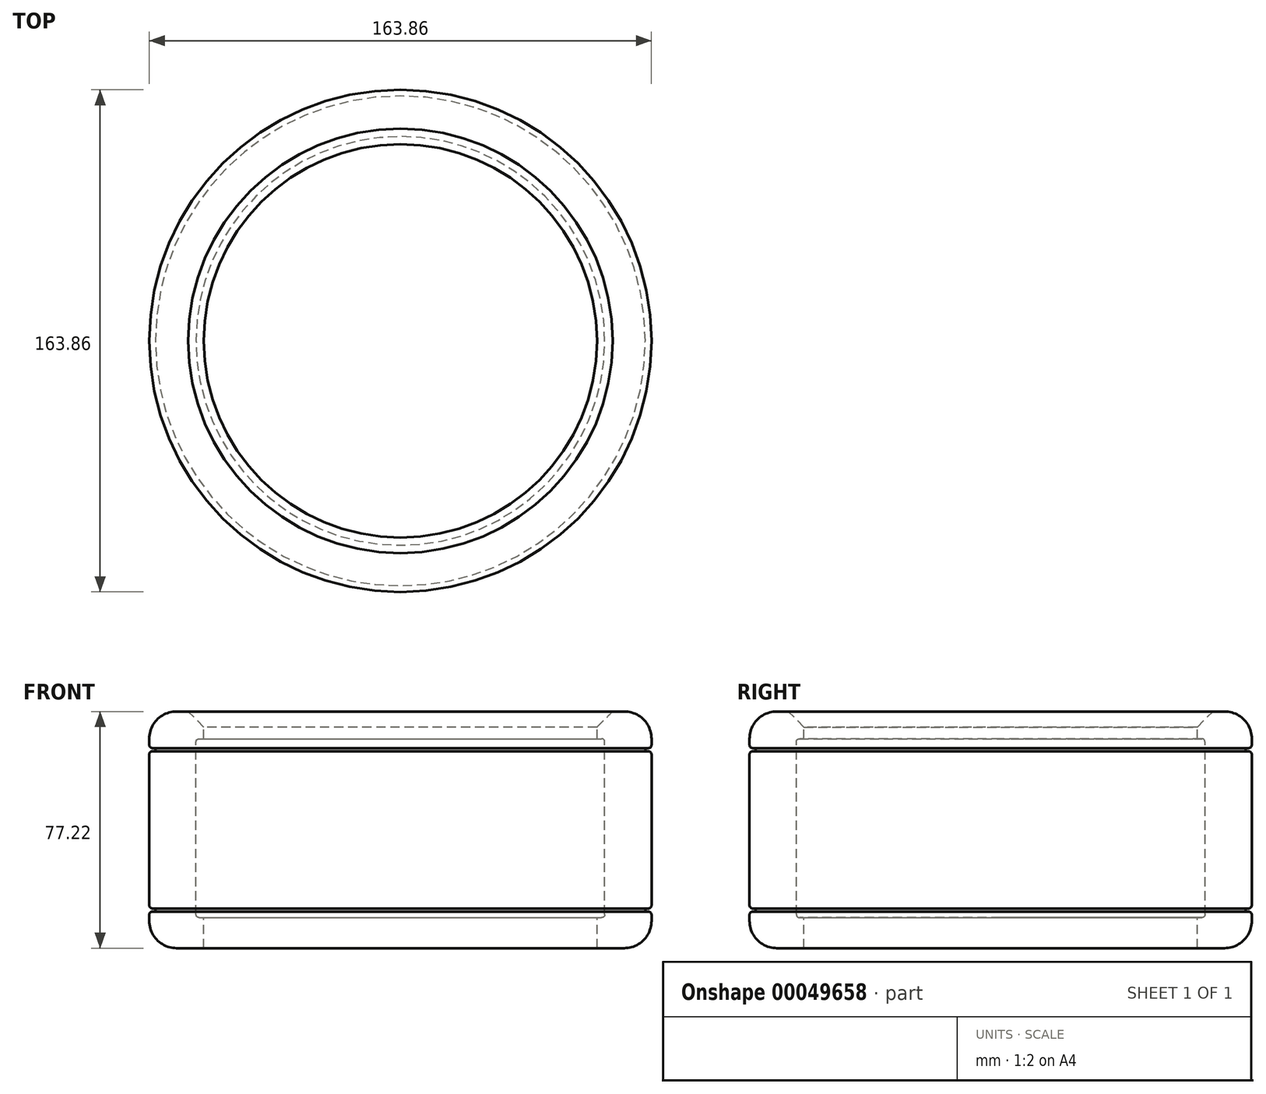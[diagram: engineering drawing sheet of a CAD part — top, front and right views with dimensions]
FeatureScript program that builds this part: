
annotation { "Feature Type Name" : "Feature", "Feature Type Description" : "" }
export const myFeature = defineFeature(function(context is Context, id is Id, definition is map)
    precondition{}
    {
        {
            var Q0;
            Q0=qCreatedBy(makeId("Top.planeOp"),FACE);
            var sketch = newSketch(context, id + "F0", { "sketchPlane" : qUnion([Q0])});
            skCircle(sketch, "E0", {"center": v(0, 0) * mm, "radius": 82.55 * mm});
            skSolve(sketch);
        }
        {
            var Q0;
            Q0=qCreatedBy(makeId("Front.planeOp"),FACE);
            var sketch = newSketch(context, id + "F1", { "sketchPlane" : qUnion([Q0])});
            skLineSegment(sketch, "E1.bottom", {"start": v(-73.04, 0) * mm, "end": v(-64.15, 0) * mm});
            skLineSegment(sketch, "E1.top", {"start": v(-73.04, 77.22) * mm, "end": v(-64.15, 77.22) * mm});
            skLineSegment(sketch, "E1.right", {"start": v(-64.15, 0) * mm, "end": v(-64.15, 9.97) * mm});
            skPoint(sketch, "E2.visualSharp", {"position": v(-81.93, 77.22) * mm});
            skArc(sketch, "E2.filletArc", {"start": v(-73.04, 77.22) * mm, "mid": v(-79.33, 74.61) * mm, "end": v(-81.93, 68.33) * mm});
            skPoint(sketch, "E3.visualSharp", {"position": v(-81.93, 0) * mm});
            skArc(sketch, "E3.filletArc", {"start": v(-81.93, 8.89) * mm, "mid": v(-79.33, 2.6) * mm, "end": v(-73.04, 0) * mm});
            skLineSegment(sketch, "E4.trimOffspring", {"start": v(-64.15, 68.33) * mm, "end": v(-64.15, 77.22) * mm});
            skLineSegment(sketch, "E5", {"start": v(-80.92, 11.94) * mm, "end": v(-79.9, 11.94) * mm});
            skLineSegment(sketch, "E6", {"start": v(-79.9, 11.94) * mm, "end": v(-79.9, 12.95) * mm});
            skLineSegment(sketch, "E7", {"start": v(-79.9, 12.95) * mm, "end": v(-80.92, 12.95) * mm});
            skLineSegment(sketch, "E8", {"start": v(-81.93, 68.33) * mm, "end": v(-81.93, 66.3) * mm});
            skLineSegment(sketch, "E9", {"start": v(-80.92, 65.28) * mm, "end": v(-79.9, 65.28) * mm});
            skLineSegment(sketch, "E10", {"start": v(-79.9, 65.28) * mm, "end": v(-79.9, 64.26) * mm});
            skLineSegment(sketch, "E11", {"start": v(-79.9, 64.26) * mm, "end": v(-80.92, 64.26) * mm});
            skPoint(sketch, "E12.visualSharp", {"position": v(-81.93, 65.28) * mm});
            skArc(sketch, "E12.filletArc", {"start": v(-81.93, 66.3) * mm, "mid": v(-81.64, 65.58) * mm, "end": v(-80.92, 65.28) * mm});
            skPoint(sketch, "E13.visualSharp", {"position": v(-81.93, 64.26) * mm});
            skArc(sketch, "E13.filletArc", {"start": v(-80.92, 64.26) * mm, "mid": v(-81.64, 63.96) * mm, "end": v(-81.93, 63.25) * mm});
            skPoint(sketch, "E14.visualSharp", {"position": v(-81.93, 12.95) * mm});
            skArc(sketch, "E14.filletArc", {"start": v(-81.93, 13.97) * mm, "mid": v(-81.64, 13.25) * mm, "end": v(-80.92, 12.95) * mm});
            skPoint(sketch, "E15.visualSharp", {"position": v(-81.93, 11.94) * mm});
            skArc(sketch, "E15.filletArc", {"start": v(-80.92, 11.94) * mm, "mid": v(-81.64, 11.64) * mm, "end": v(-81.93, 10.92) * mm});
            skLineSegment(sketch, "E16", {"start": v(-66.68, 67.3) * mm, "end": v(-66.68, 10.99) * mm});
            skLineSegment(sketch, "E17.trimOffspring", {"start": v(-65.66, 68.33) * mm, "end": v(-64.15, 68.33) * mm});
            skLineSegment(sketch, "E18.trimOffspring", {"start": v(-65.66, 9.97) * mm, "end": v(-64.15, 9.97) * mm});
            skPoint(sketch, "E19.visualSharp", {"position": v(-66.68, 9.97) * mm});
            skArc(sketch, "E19.filletArc", {"start": v(-66.68, 10.99) * mm, "mid": v(-66.38, 10.27) * mm, "end": v(-65.66, 9.97) * mm});
            skPoint(sketch, "E20.visualSharp", {"position": v(-66.68, 68.33) * mm});
            skArc(sketch, "E20.filletArc", {"start": v(-65.66, 68.33) * mm, "mid": v(-66.38, 68.03) * mm, "end": v(-66.68, 67.3) * mm});
            skLineSegment(sketch, "E21", {"start": v(-81.93, 10.92) * mm, "end": v(-81.93, 8.89) * mm});
            skLineSegment(sketch, "E22", {"start": v(-81.93, 63.25) * mm, "end": v(-81.93, 13.97) * mm});
            skSolve(sketch);
        }
        {
            var Q0;
            Q0=makeQuery(id+"F1.imprint","IMPRINT",FACE,{"disambiguationData":[TD([[makeQuery(id+"F1.imprint","IMPRINT",EDGE,{"derivedFrom":sQuery(id+"F1.wireOp",EDGE,"E1.bottom")}),1.0]])]});
            var Q1;
            Q1=sQuery(id+"F0.wireOp",EDGE,"E0");
            sweep(context, id + "F2", {"profiles" : qUnion([Q0]), "path" : qUnion([Q1])});
        }
        {
            var Q0;
            Q0=makeQuery(id+"F2.opSweep","SWEPT_EDGE",EDGE,{"disambiguationData":[OSD([sQuery(id+"F0.wireOp",EDGE,"E0"),sQuery(id+"F1.wireOp",EDGE,"E1.top"),sQuery(id+"F1.wireOp",EDGE,"E4.trimOffspring")])]});
            chamfer(context, id + "F3", {"entities" : qUnion([Q0]), "width" : 5.08 * mm, "tangentPropagation" : true});
        }
    });
